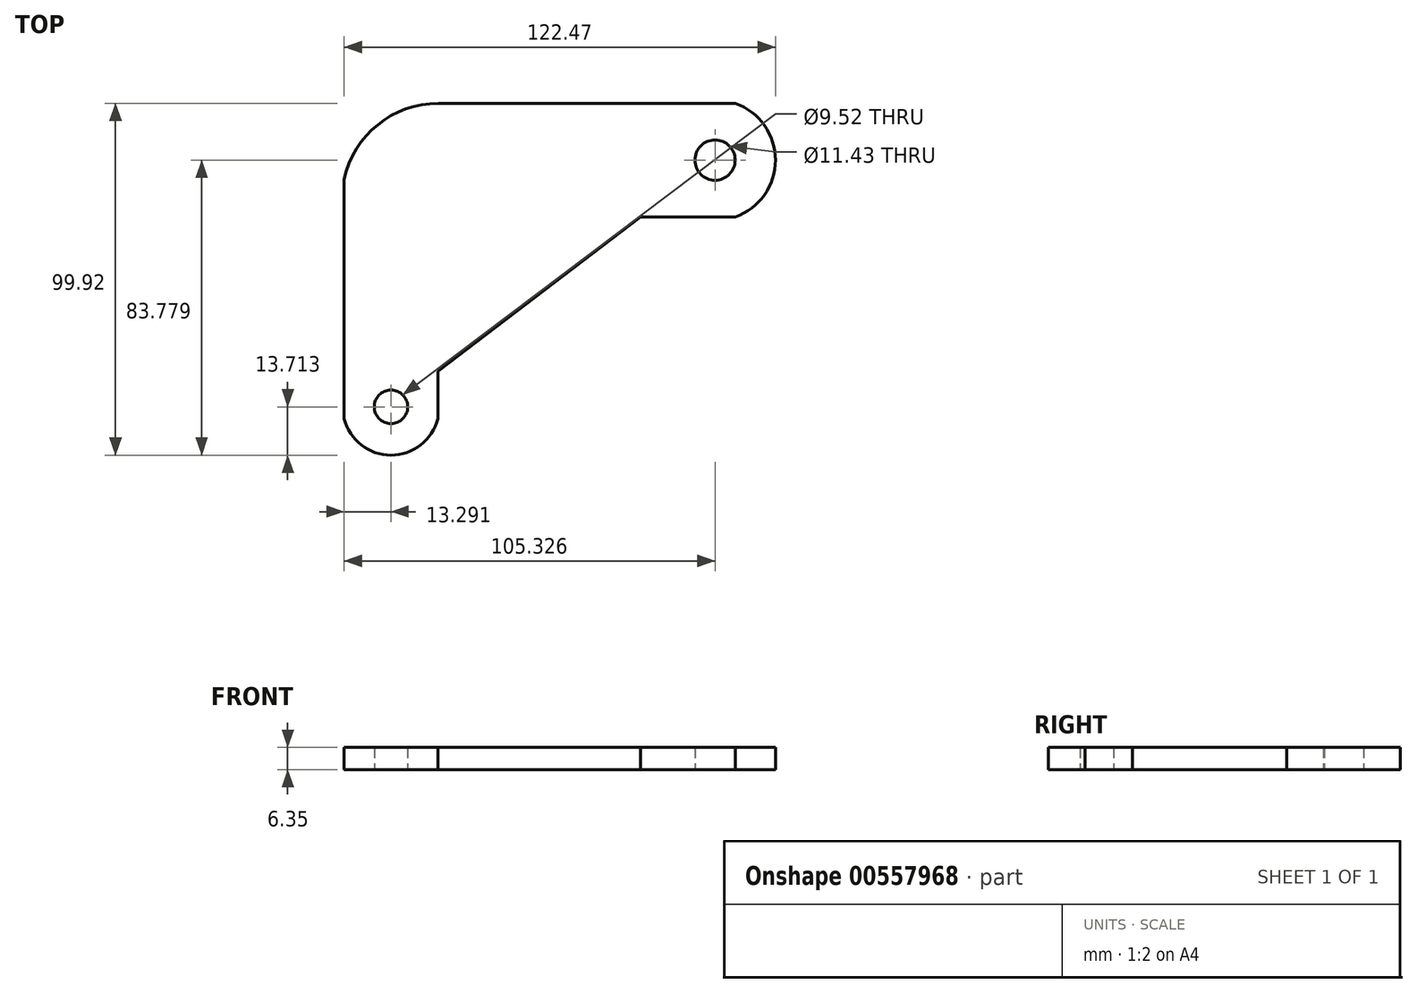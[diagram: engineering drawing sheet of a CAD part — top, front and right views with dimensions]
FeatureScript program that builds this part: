
annotation { "Feature Type Name" : "Feature", "Feature Type Description" : "" }
export const myFeature = defineFeature(function(context is Context, id is Id, definition is map)
    precondition{}
    {
        {
            var Q0;
            Q0=qCreatedBy(makeId("Top.planeOp"),FACE);
            var sketch = newSketch(context, id + "F0", { "sketchPlane" : qUnion([Q0])});
            skArc(sketch, "E0", {"start": v(-28.97, -4.43) * mm, "mid": v(-22.24, 19.1) * mm, "end": v(0, 29.3) * mm});
            skLineSegment(sketch, "E1", {"start": v(-28.97, -4.43) * mm, "end": v(-28.97, -20.43) * mm});
            skLineSegment(sketch, "E2", {"start": v(0, 29.3) * mm, "end": v(55.55, 29.3) * mm});
            skArc(sketch, "E3", {"start": v(55.55, 29.3) * mm, "mid": v(66.92, 45.45) * mm, "end": v(55.55, 61.6) * mm});
            skLineSegment(sketch, "E4", {"start": v(55.55, 61.6) * mm, "end": v(-28.78, 61.6) * mm});
            skArc(sketch, "E5", {"start": v(-28.78, 61.6) * mm, "mid": v(-45.97, 55.52) * mm, "end": v(-55.55, 40) * mm});
            skLineSegment(sketch, "E6", {"start": v(-55.55, 40) * mm, "end": v(-55.55, -22.45) * mm});
            skCircle(sketch, "E7", {"center": v(49.78, 45.45) * mm, "radius": 5.72 * mm});
            skCircle(sketch, "E8", {"center": v(-42.26, -24.62) * mm, "radius": 4.76 * mm});
            skLineSegment(sketch, "E9", {"start": v(-55.55, -22.45) * mm, "end": v(-55.55, -28) * mm});
            skLineSegment(sketch, "E10", {"start": v(-28.97, -20.43) * mm, "end": v(-28.97, -28) * mm});
            skArc(sketch, "E11", {"start": v(-55.55, -28) * mm, "mid": v(-42.26, -38.33) * mm, "end": v(-28.97, -28) * mm});
            skLineSegment(sketch, "E12", {"start": v(49.78, 45.45) * mm, "end": v(-42.26, -24.62) * mm});
            skSolve(sketch);
        }
        {
            var Q0;
            Q0 = qSketchRegion(id + "F0", true);
            extrude(context, id + "F1", {"entities" : qUnion([Q0]), "depth" : 6.35 * mm, "offsetDistance" : 25.4 * mm});
        }
    });
